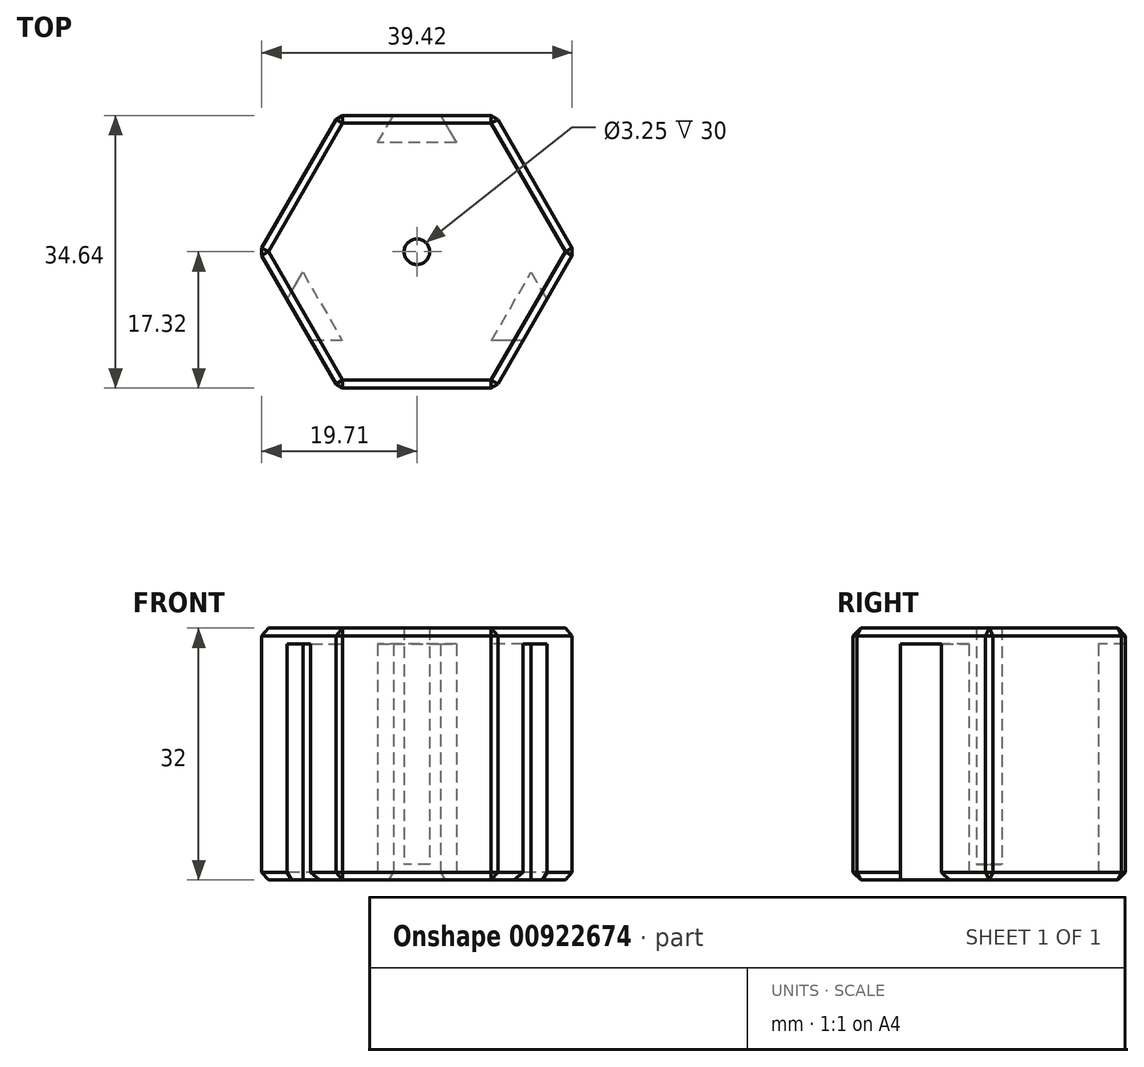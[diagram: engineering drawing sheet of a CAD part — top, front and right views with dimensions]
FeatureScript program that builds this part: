
annotation { "Feature Type Name" : "Feature", "Feature Type Description" : "" }
export const myFeature = defineFeature(function(context is Context, id is Id, definition is map)
    precondition{}
    {
        {
            var Q0;
            Q0=qCreatedBy(makeId("Top.planeOp"),FACE);
            var sketch = newSketch(context, id + "F0", { "sketchPlane" : qUnion([Q0])});
            skCircle(sketch, "E0.cCircle", {"center": v(0, 0) * mm, "radius": 20 * mm, "construction": true});
            skLineSegment(sketch, "E0.0", {"start": v(20, 0) * mm, "end": v(10, -17.32) * mm});
            skLineSegment(sketch, "E0.1", {"start": v(10, -17.32) * mm, "end": v(-10, -17.32) * mm});
            skLineSegment(sketch, "E0.2", {"start": v(-10, -17.32) * mm, "end": v(-20, 0) * mm});
            skLineSegment(sketch, "E0.3", {"start": v(-20, 0) * mm, "end": v(-10, 17.32) * mm});
            skLineSegment(sketch, "E0.4", {"start": v(-10, 17.32) * mm, "end": v(10, 17.32) * mm});
            skLineSegment(sketch, "E0.5", {"start": v(10, 17.32) * mm, "end": v(20, 0) * mm});
            skLineSegment(sketch, "E1", {"start": v(-3, 17.32) * mm, "end": v(3, 17.32) * mm});
            skLineSegment(sketch, "E2", {"start": v(3, 17.32) * mm, "end": v(5, 13.86) * mm});
            skLineSegment(sketch, "E3", {"start": v(5, 13.86) * mm, "end": v(-5, 13.86) * mm});
            skLineSegment(sketch, "E4", {"start": v(-5, 13.86) * mm, "end": v(-3, 17.32) * mm});
            skLineSegment(sketch, "E5.1.0", {"start": v(-9.5, -11.26) * mm, "end": v(-13.5, -11.26) * mm});
            skLineSegment(sketch, "E5.1.1", {"start": v(-14.5, -2.6) * mm, "end": v(-9.5, -11.26) * mm});
            skLineSegment(sketch, "E5.1.2", {"start": v(-16.5, -6.06) * mm, "end": v(-14.5, -2.6) * mm});
            skLineSegment(sketch, "E5.1.3", {"start": v(-13.5, -11.26) * mm, "end": v(-16.5, -6.06) * mm});
            skLineSegment(sketch, "E5.2.0", {"start": v(14.5, -2.6) * mm, "end": v(16.5, -6.06) * mm});
            skLineSegment(sketch, "E5.2.1", {"start": v(9.5, -11.26) * mm, "end": v(14.5, -2.6) * mm});
            skLineSegment(sketch, "E5.2.2", {"start": v(13.5, -11.26) * mm, "end": v(9.5, -11.26) * mm});
            skLineSegment(sketch, "E5.2.3", {"start": v(16.5, -6.06) * mm, "end": v(13.5, -11.26) * mm});
            skCircle(sketch, "E6", {"center": v(0, 0) * mm, "radius": 1.63 * mm});
            skSolve(sketch);
        }
        {
            var Q0;
            {var subQ9=sQuery(id+"F0.wireOp",EDGE,"E0.1");Q0=makeQuery(id+"F0.imprint","IMPRINT",FACE,{"disambiguationData":[TD([[makeQuery(id+"F0.imprint","IMPRINT",EDGE,{"derivedFrom":subQ9}),-1.0]])]});}
            extrude(context, id + "F1", {"entities" : qUnion([Q0]), "depth" : 32 * mm, "offsetDistance" : 25 * mm});
        }
        {
            var Q0;
            {var subQ2=sQuery(id+"F0.wireOp",EDGE,"E5.1.0");Q0=makeQuery(id+"F0.imprint","IMPRINT",FACE,{"disambiguationData":[TD([[makeQuery(id+"F0.imprint","IMPRINT",EDGE,{"derivedFrom":subQ2}),-1.0]])]});}
            var Q1;
            {var subQ2=sQuery(id+"F0.wireOp",EDGE,"E5.2.0");Q1=makeQuery(id+"F0.imprint","IMPRINT",FACE,{"disambiguationData":[TD([[makeQuery(id+"F0.imprint","IMPRINT",EDGE,{"derivedFrom":subQ2}),-1.0]])]});}
            var Q2;
            {var subQ0=sQuery(id+"F0.wireOp",EDGE,"E2");Q2=makeQuery(id+"F0.imprint","IMPRINT",FACE,{"disambiguationData":[TD([[makeQuery(id+"F0.imprint","IMPRINT",EDGE,{"derivedFrom":subQ0}),-1.0]])]});}
            extrude(context, id + "F2", {"entities" : qUnion([Q0, Q1, Q2]), "operationType" : NewBodyOperationType.ADD, "depth" : 32 * mm, "offsetDistance" : 25 * mm, "hasSecondDirection" : true, "secondDirectionOppositeDirection" : false, "secondDirectionDepth" : 30 * mm});
        }
        {
            var Q0;
            Q0=makeQuery(id+"F1.opExtrude","SWEPT_EDGE",EDGE,{"disambiguationData":[OSD([sQuery(id+"F0.wireOp",EDGE,"E0.0"),sQuery(id+"F0.wireOp",EDGE,"E0.5")])]});
            var Q1;
            Q1=makeQuery(id+"F1.opExtrude","CAP_EDGE",EDGE,{"disambiguationData":[OSD([sQuery(id+"F0.wireOp",EDGE,"E0.5")])],"isStart":false});
            var Q2;
            Q2=makeQuery(id+"F1.opExtrude","SWEPT_EDGE",EDGE,{"disambiguationData":[OSD([sQuery(id+"F0.wireOp",EDGE,"E0.4"),sQuery(id+"F0.wireOp",EDGE,"E0.5")])]});
            var Q3;
            {var subQ0=sQuery(id+"F0.wireOp",EDGE,"E0.4");Q3=makeQuery(id+"F2.boolean.opBoolean","MERGE",EDGE,{"derivedFrom":[makeQuery(id+"F1.opExtrude","CAP_EDGE",EDGE,{"disambiguationData":[OSD([subQ0]),TDD([makeQuery(id+"F0.imprint","IMPRINT",EDGE,{"disambiguationData":[TD([[makeQuery(id+"F0.imprint","INTERSECT",VERTEX,{"derivedFrom":[subQ0,sQuery(id+"F0.wireOp",EDGE,"E2")]}),-1.0]])],"derivedFrom":subQ0})])],"isStart":false}),makeQuery(id+"F1.opExtrude","CAP_EDGE",EDGE,{"disambiguationData":[OSD([subQ0]),TDD([makeQuery(id+"F0.imprint","IMPRINT",EDGE,{"disambiguationData":[TD([[makeQuery(id+"F0.imprint","INTERSECT",VERTEX,{"derivedFrom":[sQuery(id+"F0.wireOp",EDGE,"E0.3"),subQ0]}),-1.0]])],"derivedFrom":subQ0})])],"isStart":false}),makeQuery(id+"F2.opExtrude","CAP_EDGE",EDGE,{"disambiguationData":[OSD([subQ0])],"isStart":false})]});}
            var Q4;
            Q4=makeQuery(id+"F1.opExtrude","SWEPT_EDGE",EDGE,{"disambiguationData":[OSD([sQuery(id+"F0.wireOp",EDGE,"E0.3"),sQuery(id+"F0.wireOp",EDGE,"E0.4")])]});
            var Q5;
            {var subQ0=sQuery(id+"F0.wireOp",EDGE,"E0.4");Q5=makeQuery(id+"F1.opExtrude","CAP_EDGE",EDGE,{"disambiguationData":[OSD([subQ0]),TDD([makeQuery(id+"F0.imprint","IMPRINT",EDGE,{"disambiguationData":[TD([[makeQuery(id+"F0.imprint","INTERSECT",VERTEX,{"derivedFrom":[sQuery(id+"F0.wireOp",EDGE,"E0.3"),subQ0]}),-1.0]])],"derivedFrom":subQ0})])],"isStart":true});}
            var Q6;
            {var subQ0=sQuery(id+"F0.wireOp",EDGE,"E0.4");Q6=makeQuery(id+"F1.opExtrude","CAP_EDGE",EDGE,{"disambiguationData":[OSD([subQ0]),TDD([makeQuery(id+"F0.imprint","IMPRINT",EDGE,{"disambiguationData":[TD([[makeQuery(id+"F0.imprint","INTERSECT",VERTEX,{"derivedFrom":[subQ0,sQuery(id+"F0.wireOp",EDGE,"E2")]}),-1.0]])],"derivedFrom":subQ0})])],"isStart":true});}
            var Q7;
            Q7=makeQuery(id+"F1.opExtrude","CAP_EDGE",EDGE,{"disambiguationData":[OSD([sQuery(id+"F0.wireOp",EDGE,"E0.5")])],"isStart":true});
            var Q8;
            {var subQ0=sQuery(id+"F0.wireOp",EDGE,"E0.0");Q8=makeQuery(id+"F2.boolean.opBoolean","MERGE",EDGE,{"derivedFrom":[makeQuery(id+"F1.opExtrude","CAP_EDGE",EDGE,{"disambiguationData":[OSD([subQ0]),TDD([makeQuery(id+"F0.imprint","IMPRINT",EDGE,{"disambiguationData":[TD([[makeQuery(id+"F0.imprint","INTERSECT",VERTEX,{"derivedFrom":[subQ0,sQuery(id+"F0.wireOp",EDGE,"E5.2.2")]}),-1.0]])],"derivedFrom":subQ0})])],"isStart":false}),makeQuery(id+"F1.opExtrude","CAP_EDGE",EDGE,{"disambiguationData":[OSD([subQ0]),TDD([makeQuery(id+"F0.imprint","IMPRINT",EDGE,{"disambiguationData":[TD([[makeQuery(id+"F0.imprint","INTERSECT",VERTEX,{"derivedFrom":[subQ0,sQuery(id+"F0.wireOp",EDGE,"E0.5")]}),-1.0]])],"derivedFrom":subQ0})])],"isStart":false}),makeQuery(id+"F2.opExtrude","CAP_EDGE",EDGE,{"disambiguationData":[OSD([subQ0])],"isStart":false})]});}
            var Q9;
            {var subQ0=sQuery(id+"F0.wireOp",EDGE,"E0.0");Q9=makeQuery(id+"F1.opExtrude","CAP_EDGE",EDGE,{"disambiguationData":[OSD([subQ0]),TDD([makeQuery(id+"F0.imprint","IMPRINT",EDGE,{"disambiguationData":[TD([[makeQuery(id+"F0.imprint","INTERSECT",VERTEX,{"derivedFrom":[subQ0,sQuery(id+"F0.wireOp",EDGE,"E0.5")]}),-1.0]])],"derivedFrom":subQ0})])],"isStart":true});}
            var Q10;
            {var subQ0=sQuery(id+"F0.wireOp",EDGE,"E0.0");Q10=makeQuery(id+"F1.opExtrude","CAP_EDGE",EDGE,{"disambiguationData":[OSD([subQ0]),TDD([makeQuery(id+"F0.imprint","IMPRINT",EDGE,{"disambiguationData":[TD([[makeQuery(id+"F0.imprint","INTERSECT",VERTEX,{"derivedFrom":[subQ0,sQuery(id+"F0.wireOp",EDGE,"E5.2.2")]}),-1.0]])],"derivedFrom":subQ0})])],"isStart":true});}
            var Q11;
            Q11=makeQuery(id+"F1.opExtrude","SWEPT_EDGE",EDGE,{"disambiguationData":[OSD([sQuery(id+"F0.wireOp",EDGE,"E0.0"),sQuery(id+"F0.wireOp",EDGE,"E0.1")])]});
            var Q12;
            Q12=makeQuery(id+"F1.opExtrude","CAP_EDGE",EDGE,{"disambiguationData":[OSD([sQuery(id+"F0.wireOp",EDGE,"E0.1")])],"isStart":false});
            var Q13;
            Q13=makeQuery(id+"F1.opExtrude","CAP_EDGE",EDGE,{"disambiguationData":[OSD([sQuery(id+"F0.wireOp",EDGE,"E0.1")])],"isStart":true});
            var Q14;
            {var subQ0=sQuery(id+"F0.wireOp",EDGE,"E0.2");Q14=makeQuery(id+"F1.opExtrude","CAP_EDGE",EDGE,{"disambiguationData":[OSD([subQ0]),TDD([makeQuery(id+"F0.imprint","IMPRINT",EDGE,{"disambiguationData":[TD([[makeQuery(id+"F0.imprint","INTERSECT",VERTEX,{"derivedFrom":[sQuery(id+"F0.wireOp",EDGE,"E0.1"),subQ0]}),-1.0]])],"derivedFrom":subQ0})])],"isStart":true});}
            var Q15;
            Q15=makeQuery(id+"F1.opExtrude","SWEPT_EDGE",EDGE,{"disambiguationData":[OSD([sQuery(id+"F0.wireOp",EDGE,"E0.1"),sQuery(id+"F0.wireOp",EDGE,"E0.2")])]});
            var Q16;
            {var subQ0=sQuery(id+"F0.wireOp",EDGE,"E0.2");Q16=makeQuery(id+"F2.boolean.opBoolean","MERGE",EDGE,{"derivedFrom":[makeQuery(id+"F1.opExtrude","CAP_EDGE",EDGE,{"disambiguationData":[OSD([subQ0]),TDD([makeQuery(id+"F0.imprint","IMPRINT",EDGE,{"disambiguationData":[TD([[makeQuery(id+"F0.imprint","INTERSECT",VERTEX,{"derivedFrom":[sQuery(id+"F0.wireOp",EDGE,"E0.1"),subQ0]}),-1.0]])],"derivedFrom":subQ0})])],"isStart":false}),makeQuery(id+"F1.opExtrude","CAP_EDGE",EDGE,{"disambiguationData":[OSD([subQ0]),TDD([makeQuery(id+"F0.imprint","IMPRINT",EDGE,{"disambiguationData":[TD([[makeQuery(id+"F0.imprint","INTERSECT",VERTEX,{"derivedFrom":[subQ0,sQuery(id+"F0.wireOp",EDGE,"E5.1.2")]}),-1.0]])],"derivedFrom":subQ0})])],"isStart":false}),makeQuery(id+"F2.opExtrude","CAP_EDGE",EDGE,{"disambiguationData":[OSD([subQ0])],"isStart":false})]});}
            var Q17;
            Q17=makeQuery(id+"F1.opExtrude","SWEPT_EDGE",EDGE,{"disambiguationData":[OSD([sQuery(id+"F0.wireOp",EDGE,"E0.2"),sQuery(id+"F0.wireOp",EDGE,"E0.3")])]});
            var Q18;
            {var subQ0=sQuery(id+"F0.wireOp",EDGE,"E0.2");Q18=makeQuery(id+"F1.opExtrude","CAP_EDGE",EDGE,{"disambiguationData":[OSD([subQ0]),TDD([makeQuery(id+"F0.imprint","IMPRINT",EDGE,{"disambiguationData":[TD([[makeQuery(id+"F0.imprint","INTERSECT",VERTEX,{"derivedFrom":[subQ0,sQuery(id+"F0.wireOp",EDGE,"E5.1.2")]}),-1.0]])],"derivedFrom":subQ0})])],"isStart":true});}
            var Q19;
            Q19=makeQuery(id+"F1.opExtrude","CAP_EDGE",EDGE,{"disambiguationData":[OSD([sQuery(id+"F0.wireOp",EDGE,"E0.3")])],"isStart":true});
            var Q20;
            Q20=makeQuery(id+"F1.opExtrude","CAP_EDGE",EDGE,{"disambiguationData":[OSD([sQuery(id+"F0.wireOp",EDGE,"E0.3")])],"isStart":false});
            chamfer(context, id + "F3", {"entities" : qUnion([Q0, Q1, Q2, Q3, Q4, Q5, Q6, Q7, Q8, Q9, Q10, Q11, Q12, Q13, Q14, Q15, Q16, Q17, Q18, Q19, Q20]), "width" : 1 * mm, "tangentPropagation" : true});
        }
        {
            var Q0;
            Q0=makeQuery(id+"F0.imprint","IMPRINT",FACE,{"disambiguationData":[TD([[makeQuery(id+"F0.imprint","IMPRINT",EDGE,{"derivedFrom":sQuery(id+"F0.wireOp",EDGE,"E6")}),1.0]])]});
            extrude(context, id + "F4", {"entities" : qUnion([Q0]), "operationType" : NewBodyOperationType.ADD, "depth" : 2 * mm, "offsetDistance" : 25 * mm});
        }
    });
